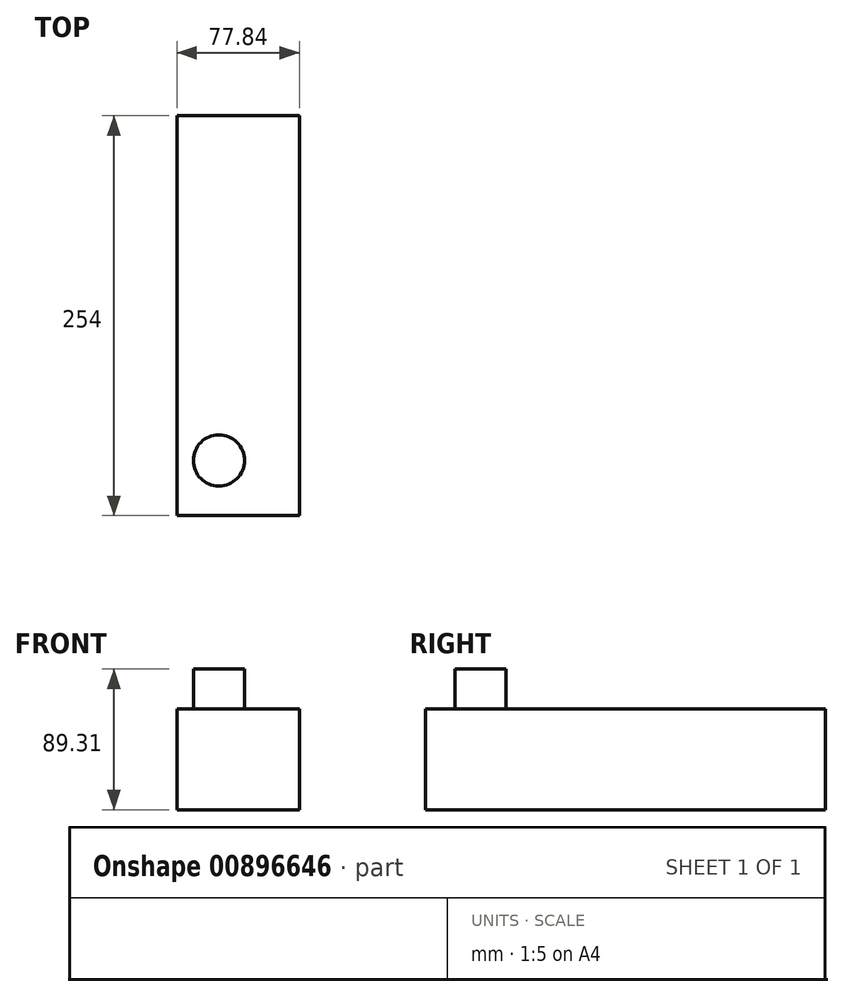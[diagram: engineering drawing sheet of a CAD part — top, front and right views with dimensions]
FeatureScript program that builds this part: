
annotation { "Feature Type Name" : "Feature", "Feature Type Description" : "" }
export const myFeature = defineFeature(function(context is Context, id is Id, definition is map)
    precondition{}
    {
        {
            var Q0;
            Q0=qCreatedBy(makeId("Front.planeOp"),FACE);
            var sketch = newSketch(context, id + "F0", { "sketchPlane" : qUnion([Q0])});
            skLineSegment(sketch, "E0", {"start": v(-45.35, 51.27) * mm, "end": v(-45.35, -12.64) * mm});
            skLineSegment(sketch, "E1", {"start": v(-45.35, -12.64) * mm, "end": v(32.49, -12.64) * mm});
            skLineSegment(sketch, "E2", {"start": v(32.49, -12.64) * mm, "end": v(32.49, 51.27) * mm});
            skLineSegment(sketch, "E3", {"start": v(32.49, 51.27) * mm, "end": v(-45.35, 51.27) * mm});
            skSolve(sketch);
        }
        {
            var Q0;
            Q0 = qSketchRegion(id + "F0", true);
            extrude(context, id + "F1", {"entities" : qUnion([Q0]), "endBound" : BoundingType.SYMMETRIC, "depth" : 254 * mm, "offsetDistance" : 25.4 * mm});
        }
        {
            var Q0;
            Q0=makeQuery(id+"F1.opExtrude","SWEPT_FACE",FACE,{"disambiguationData":[OSD([sQuery(id+"F0.wireOp",EDGE,"E3")])]});
            var sketch = newSketch(context, id + "F2", { "sketchPlane" : qUnion([Q0])});
            skCircle(sketch, "E4", {"center": v(-18.65, -91.96) * mm, "radius": 16.26 * mm});
            skSolve(sketch);
        }
        {
            var Q0;
            Q0 = qSketchRegion(id + "F2", true);
            extrude(context, id + "F3", {"entities" : qUnion([Q0]), "depth" : 25.4 * mm, "offsetDistance" : 25.4 * mm});
        }
    });
